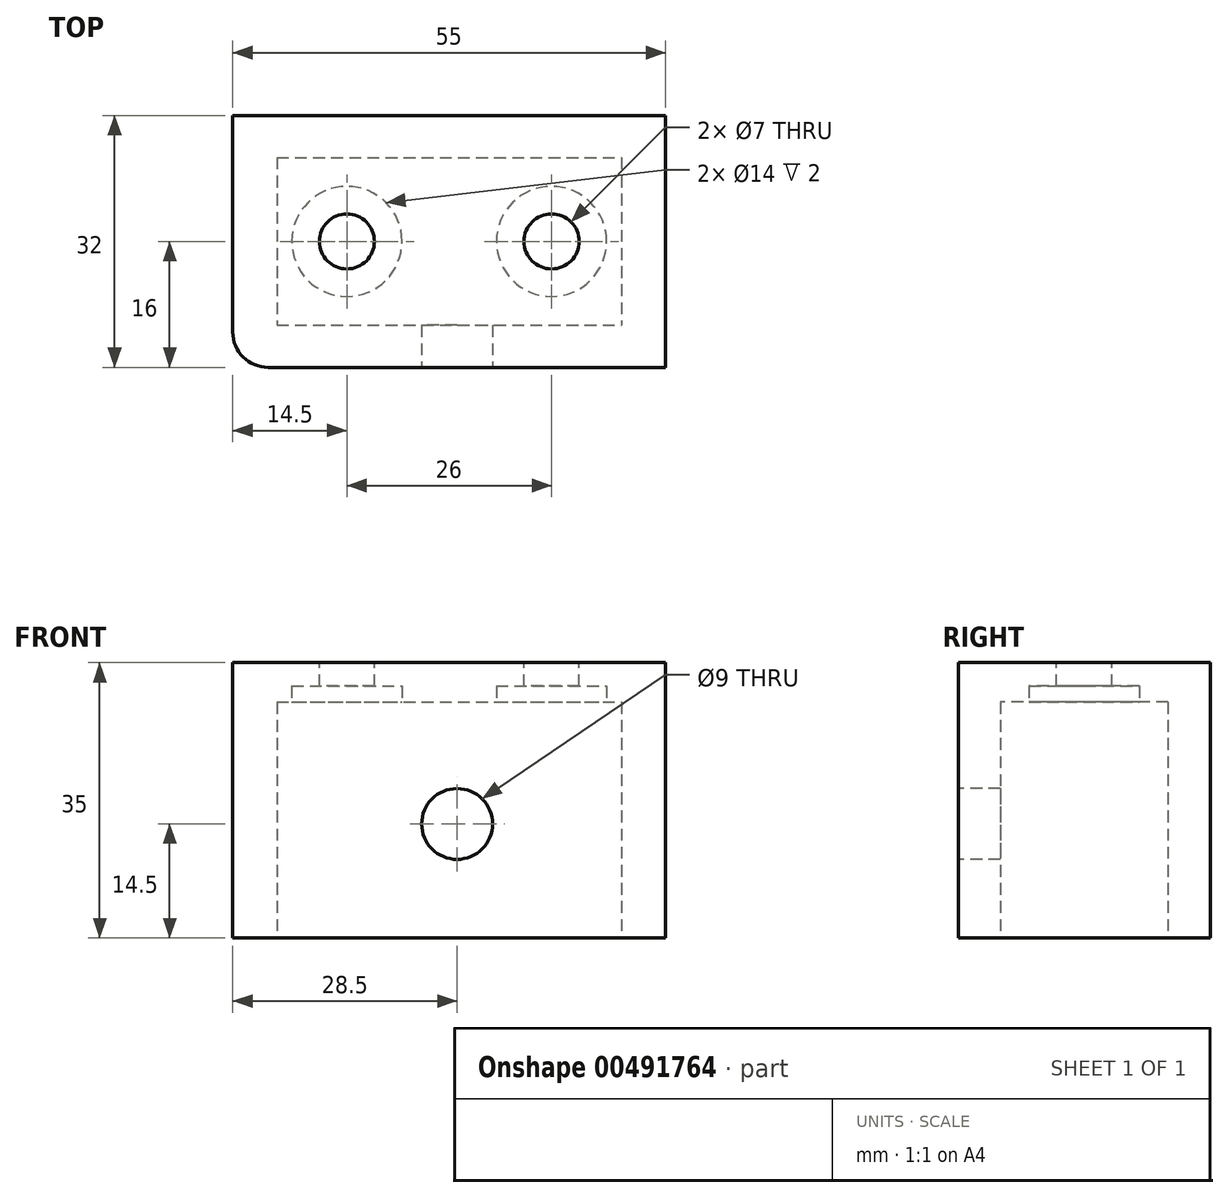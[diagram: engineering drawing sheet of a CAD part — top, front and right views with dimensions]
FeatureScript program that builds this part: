
annotation { "Feature Type Name" : "Feature", "Feature Type Description" : "" }
export const myFeature = defineFeature(function(context is Context, id is Id, definition is map)
    precondition{}
    {
        {
            var Q0;
            Q0=qCreatedBy(makeId("Top.planeOp"),FACE);
            var sketch = newSketch(context, id + "F0", { "sketchPlane" : qUnion([Q0])});
            skCircle(sketch, "E0", {"center": v(-33.3, 30.83) * mm, "radius": 5 * mm});
            skLineSegment(sketch, "E1.bottom", {"start": v(-27.5, 16) * mm, "end": v(27.5, 16) * mm});
            skLineSegment(sketch, "E1.top", {"start": v(-27.5, -16) * mm, "end": v(27.5, -16) * mm});
            skLineSegment(sketch, "E1.left", {"start": v(-27.5, 16) * mm, "end": v(-27.5, -16) * mm});
            skLineSegment(sketch, "E1.right", {"start": v(27.5, 16) * mm, "end": v(27.5, -16) * mm});
            skPoint(sketch, "E1.middle", {"position": v(0, 0) * mm});
            skSolve(sketch);
        }
        {
            var Q0;
            Q0=makeQuery(id+"F0.imprint","IMPRINT",FACE,{"disambiguationData":[TD([[makeQuery(id+"F0.imprint","IMPRINT",EDGE,{"derivedFrom":sQuery(id+"F0.wireOp",EDGE,"E1.bottom")}),-1.0]])]});
            extrude(context, id + "F1", {"entities" : qUnion([Q0]), "depth" : 35 * mm});
        }
        {
            var Q0;
            Q0=qCreatedBy(makeId("Top.planeOp"),FACE);
            var sketch = newSketch(context, id + "F2", { "sketchPlane" : qUnion([Q0])});
            skLineSegment(sketch, "E2.bottom", {"start": v(-21.89, 10.65) * mm, "end": v(21.89, 10.65) * mm});
            skLineSegment(sketch, "E2.top", {"start": v(-21.89, -10.65) * mm, "end": v(21.89, -10.65) * mm});
            skLineSegment(sketch, "E2.left", {"start": v(-21.89, 10.65) * mm, "end": v(-21.89, -10.65) * mm});
            skLineSegment(sketch, "E2.right", {"start": v(21.89, 10.65) * mm, "end": v(21.89, -10.65) * mm});
            skPoint(sketch, "E2.middle", {"position": v(0, 0) * mm});
            skSolve(sketch);
        }
        {
            var Q0;
            Q0=makeQuery(id+"F2.imprint","IMPRINT",FACE,{"disambiguationData":[TD([[makeQuery(id+"F2.imprint","IMPRINT",EDGE,{"derivedFrom":sQuery(id+"F2.wireOp",EDGE,"E2.bottom")}),-1.0]])]});
            extrude(context, id + "F3", {"entities" : qUnion([Q0]), "operationType" : NewBodyOperationType.REMOVE, "depth" : 30 * mm});
        }
        {
            var Q0;
            Q0=makeQuery(id+"F1.opExtrude","SWEPT_EDGE",EDGE,{"disambiguationData":[OSD([sQuery(id+"F0.wireOp",EDGE,"E1.top"),sQuery(id+"F0.wireOp",EDGE,"E1.left")])]});
            fillet(context, id + "F4", {"entities" : qUnion([Q0]), "radius" : 4.5 * mm, "tangentPropagation" : true, "allowEdgeOverflow" : false});
        }
        {
            var Q0;
            Q0=makeQuery(id+"F1.opExtrude","SWEPT_FACE",FACE,{"disambiguationData":[OSD([sQuery(id+"F0.wireOp",EDGE,"E1.top")])]});
            var sketch = newSketch(context, id + "F5", { "sketchPlane" : qUnion([Q0])});
            skCircle(sketch, "E3", {"center": v(1, 14.5) * mm, "radius": 4.5 * mm});
            skSolve(sketch);
        }
        {
            var Q0;
            Q0 = qSketchRegion(id + "F5", true);
            extrude(context, id + "F6", {"entities" : qUnion([Q0]), "operationType" : NewBodyOperationType.REMOVE, "oppositeDirection" : true, "depth" : 10 * mm});
        }
        {
            var Q0;
            Q0=makeQuery(id+"F1.opExtrude","CAP_FACE",FACE,{"disambiguationData":[OSD([sQuery(id+"F0.wireOp",EDGE,"E1.bottom"),sQuery(id+"F0.wireOp",EDGE,"E1.top"),sQuery(id+"F0.wireOp",EDGE,"E1.left"),sQuery(id+"F0.wireOp",EDGE,"E1.right")])],"isStart":false});
            var sketch = newSketch(context, id + "F7", { "sketchPlane" : qUnion([Q0])});
            skCircle(sketch, "E4", {"center": v(-13, 0) * mm, "radius": 3.5 * mm});
            skCircle(sketch, "E5", {"center": v(13, 0) * mm, "radius": 3.5 * mm});
            skSolve(sketch);
        }
        {
            var Q0;
            Q0=makeQuery(id+"F7.imprint","IMPRINT",FACE,{"disambiguationData":[TD([[makeQuery(id+"F7.imprint","IMPRINT",EDGE,{"derivedFrom":sQuery(id+"F7.wireOp",EDGE,"E4")}),1.0]])]});
            var Q1;
            Q1=makeQuery(id+"F7.imprint","IMPRINT",FACE,{"disambiguationData":[TD([[makeQuery(id+"F7.imprint","IMPRINT",EDGE,{"derivedFrom":sQuery(id+"F7.wireOp",EDGE,"E5")}),1.0]])]});
            extrude(context, id + "F8", {"entities" : qUnion([Q0, Q1]), "operationType" : NewBodyOperationType.REMOVE, "oppositeDirection" : true, "depth" : 3 * mm});
        }
        {
            var Q0;
            Q0=makeQuery(id+"F3.boolean.opBoolean","COPY",FACE,{"derivedFrom":makeQuery(id+"F3.opExtrude","CAP_FACE",FACE,{"disambiguationData":[OSD([sQuery(id+"F2.wireOp",EDGE,"E2.bottom"),sQuery(id+"F2.wireOp",EDGE,"E2.top"),sQuery(id+"F2.wireOp",EDGE,"E2.left"),sQuery(id+"F2.wireOp",EDGE,"E2.right")])],"isStart":false})});
            var sketch = newSketch(context, id + "F9", { "sketchPlane" : qUnion([Q0])});
            skCircle(sketch, "E6", {"center": v(-13, 0) * mm, "radius": 7 * mm});
            skCircle(sketch, "E7", {"center": v(13, 0) * mm, "radius": 7 * mm});
            skSolve(sketch);
        }
        {
            var Q0;
            Q0=makeQuery(id+"F9.imprint","IMPRINT",FACE,{"disambiguationData":[TD([[makeQuery(id+"F9.imprint","IMPRINT",EDGE,{"derivedFrom":sQuery(id+"F9.wireOp",EDGE,"E6")}),1.0]])]});
            var Q1;
            Q1=makeQuery(id+"F9.imprint","IMPRINT",FACE,{"disambiguationData":[TD([[makeQuery(id+"F9.imprint","IMPRINT",EDGE,{"derivedFrom":sQuery(id+"F9.wireOp",EDGE,"E7")}),1.0]])]});
            extrude(context, id + "F10", {"entities" : qUnion([Q0, Q1]), "operationType" : NewBodyOperationType.REMOVE, "oppositeDirection" : true, "depth" : 2 * mm});
        }
    });
